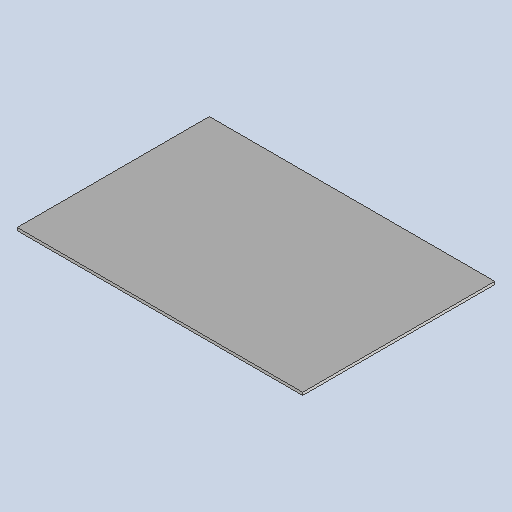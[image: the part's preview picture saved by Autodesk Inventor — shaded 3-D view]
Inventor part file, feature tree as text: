
AUTODESK INVENTOR PART (.ipt)
format: ipt  version: 2025 (Build 290162010, 162A)  size: 105,472 bytes
history: native  units: mm
features: other x2, sheet_metal_op x1, sketch x1
ambient origin geometry x8: Origin, YZ Plane, XZ Plane, XY Plane, X Axis, Y Axis, Z Axis, Center Point
bodies: Body1 (feature_tree)
feature tree (4):
  sheet_metal_op  "Face3"
  sketch  "Sketch6"  dims[d40=310.0mm d41=208.686mm d42=3.0mm]
  other  "Plate5"
  other  "Definition1"
